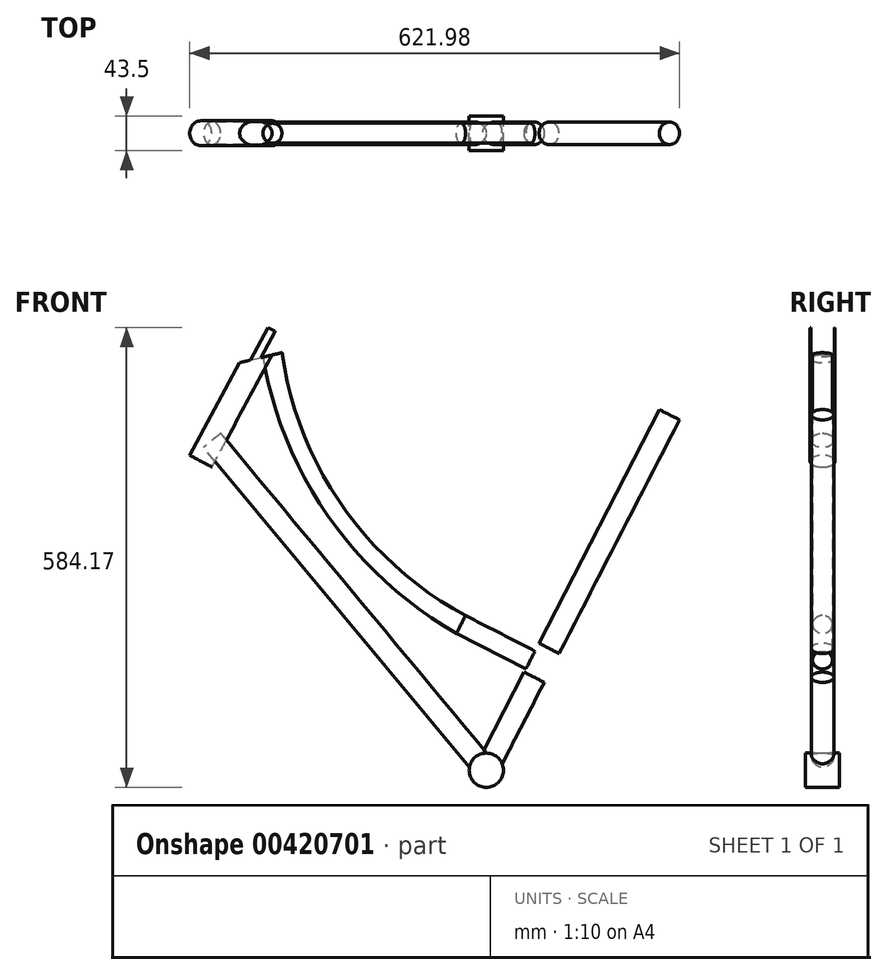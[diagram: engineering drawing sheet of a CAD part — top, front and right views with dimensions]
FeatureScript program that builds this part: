
annotation { "Feature Type Name" : "Feature", "Feature Type Description" : "" }
export const myFeature = defineFeature(function(context is Context, id is Id, definition is map)
    precondition{}
    {
        {
            var Q0;
            Q0=qCreatedBy(makeId("Front.planeOp"),FACE);
            var sketch = newSketch(context, id + "F0", { "sketchPlane" : qUnion([Q0])});
            skCircle(sketch, "E0", {"center": v(0, 0) * mm, "radius": 21.75 * mm});
            skSolve(sketch);
        }
        {
            var Q0;
            Q0=makeQuery(id+"F0.imprint","IMPRINT",FACE,{"disambiguationData":[TD([[makeQuery(id+"F0.imprint","IMPRINT",EDGE,{"derivedFrom":sQuery(id+"F0.wireOp",EDGE,"E0")}),1.0]])]});
            extrude(context, id + "F1", {"entities" : qUnion([Q0]), "depth" : 21.75 * mm});
        }
        {
            var Q0;
            Q0=makeQuery(id+"F1.opExtrude","CAP_FACE",FACE,{"disambiguationData":[OSD([sQuery(id+"F0.wireOp",EDGE,"E0")])],"isStart":true});
            extrude(context, id + "F2", {"entities" : qUnion([Q0]), "operationType" : NewBodyOperationType.ADD, "depth" : 21.75 * mm});
        }
        {
            var Q0;
            Q0=qCreatedBy(makeId("Front.planeOp"),FACE);
            var sketch = newSketch(context, id + "F3", { "sketchPlane" : qUnion([Q0])});
            skLineSegment(sketch, "E1", {"start": v(0, 0) * mm, "end": v(164.55, 0) * mm, "construction": true});
            skLineSegment(sketch, "E2", {"start": v(0, 0) * mm, "end": v(232.6, 451.62) * mm, "construction": true});
            skLineSegment(sketch, "E3", {"start": v(0, 0) * mm, "end": v(-348.5, 419.02) * mm, "construction": true});
            skLineSegment(sketch, "E4", {"start": v(-362.7, 392.6) * mm, "end": v(-272.76, 559.96) * mm, "construction": true});
            skPoint(sketch, "E5.end.orphan", {"position": v(68.68, 133.35) * mm});
            skPoint(sketch, "E5.start.orphan", {"position": v(-275.13, 555.56) * mm});
            skLineSegment(sketch, "E6", {"start": v(68.68, 133.35) * mm, "end": v(-32.16, 185.29) * mm, "construction": true});
            skArc(sketch, "E7", {"start": v(-275.13, 555.56) * mm, "mid": v(-202.35, 338.46) * mm, "end": v(-32.16, 185.29) * mm, "construction": true});
            skSolve(sketch);
        }
        {
            var Q0;
            Q0=sQuery(id+"F3.wireOp",VERTEX,"E2.end");
            var Q1;
            Q1=sQuery(id+"F3.wireOp",EDGE,"E2");
            cPlane(context, id + "F4", {"entities" : qUnion([Q0, Q1]), "cplaneType" : CPlaneType.LINE_POINT, "offset" : 25 * mm, "width" : 150 * mm, "height" : 150 * mm});
        }
        {
            var Q0;
            Q0=qCreatedBy(id+"F4.planeOp",FACE);
            var sketch = newSketch(context, id + "F5", { "sketchPlane" : qUnion([Q0])});
            skCircle(sketch, "E8", {"center": v(0, 0) * mm, "radius": 14.29 * mm});
            skSolve(sketch);
        }
        {
            var Q0;
            Q0 = qSketchRegion(id + "F5", true);
            extrude(context, id + "F6", {"entities" : qUnion([Q0]), "endBound" : BoundingType.UP_TO_NEXT, "oppositeDirection" : true, "depth" : 25 * mm});
        }
        {
            var Q0;
            Q0=sQuery(id+"F3.wireOp",VERTEX,"E4.end");
            var Q1;
            Q1=sQuery(id+"F3.wireOp",EDGE,"E4");
            cPlane(context, id + "F7", {"entities" : qUnion([Q0, Q1]), "cplaneType" : CPlaneType.LINE_POINT, "offset" : 25 * mm, "width" : 150 * mm, "height" : 150 * mm});
        }
        {
            var Q0;
            Q0=qCreatedBy(id+"F7.planeOp",FACE);
            var sketch = newSketch(context, id + "F8", { "sketchPlane" : qUnion([Q0])});
            skCircle(sketch, "E9", {"center": v(-505.32, 0) * mm, "radius": 15.88 * mm});
            skSolve(sketch);
        }
        {
            var Q0;
            Q0=makeQuery(id+"F8.imprint","IMPRINT",FACE,{"disambiguationData":[TD([[makeQuery(id+"F8.imprint","IMPRINT",EDGE,{"derivedFrom":sQuery(id+"F8.wireOp",EDGE,"E9")}),1.0]])]});
            extrude(context, id + "F9", {"entities" : qUnion([Q0]), "oppositeDirection" : true, "depth" : 190 * mm});
        }
        {
            var Q0;
            Q0=sQuery(id+"F3.wireOp",VERTEX,"E3.end");
            var Q1;
            Q1=sQuery(id+"F3.wireOp",EDGE,"E3");
            cPlane(context, id + "F10", {"entities" : qUnion([Q0, Q1]), "cplaneType" : CPlaneType.LINE_POINT, "offset" : 25 * mm, "width" : 150 * mm, "height" : 150 * mm});
        }
        {
            var Q0;
            Q0=qCreatedBy(id+"F10.planeOp",FACE);
            var sketch = newSketch(context, id + "F11", { "sketchPlane" : qUnion([Q0])});
            skCircle(sketch, "E10", {"center": v(0, 0) * mm, "radius": 14.29 * mm});
            skSolve(sketch);
        }
        {
            var Q0;
            Q0 = qSketchRegion(id + "F11", true);
            var Q1;
            {var subQ0=sQuery(id+"F0.wireOp",EDGE,"E0");Q1=makeQuery(id+"F2.boolean.opBoolean","MERGE",FACE,{"derivedFrom":[makeQuery(id+"F1.opExtrude","SWEPT_FACE",FACE,{"disambiguationData":[OSD([subQ0])]}),makeQuery(id+"F2.opExtrude","SWEPT_FACE",FACE,{"disambiguationData":[OSD([subQ0])]})]});}
            extrude(context, id + "F12", {"entities" : qUnion([Q0]), "endBound" : BoundingType.UP_TO_SURFACE, "oppositeDirection" : true, "endBoundEntityFace" : qUnion([Q1]), "depth" : 25 * mm});
        }
        {
            var Q0;
            Q0=sQuery(id+"F3.wireOp",VERTEX,"E5.start.orphan");
            var Q1;
            Q1=sQuery(id+"F3.wireOp",EDGE,"E7");
            cPlane(context, id + "F13", {"entities" : qUnion([Q0, Q1]), "cplaneType" : CPlaneType.CURVE_POINT, "offset" : 25 * mm, "width" : 150 * mm, "height" : 150 * mm});
        }
        {
            var Q0;
            Q0=sQuery(id+"F3.wireOp",VERTEX,"E7.end");
            var Q1;
            Q1=sQuery(id+"F3.wireOp",EDGE,"E7");
            cPlane(context, id + "F14", {"entities" : qUnion([Q0, Q1]), "cplaneType" : CPlaneType.CURVE_POINT, "offset" : 25 * mm, "width" : 150 * mm, "height" : 150 * mm});
        }
        {
            var Q0;
            Q0=qCreatedBy(id+"F13.planeOp",FACE);
            var sketch = newSketch(context, id + "F15", { "sketchPlane" : qUnion([Q0])});
            skCircle(sketch, "E11", {"center": v(-237.75, 0) * mm, "radius": 12.7 * mm});
            skSolve(sketch);
        }
        {
            var Q0;
            Q0=qCreatedBy(id+"F14.planeOp",FACE);
            var sketch = newSketch(context, id + "F16", { "sketchPlane" : qUnion([Q0])});
            skCircle(sketch, "E12", {"center": v(0, 150) * mm, "radius": 12.7 * mm});
            skSolve(sketch);
        }
        {
            var Q0;
            Q0=qCreatedBy(makeId("Front.planeOp"),FACE);
            var sketch = newSketch(context, id + "F17", { "sketchPlane" : qUnion([Q0])});
            skArc(sketch, "E13", {"start": v(-262.46, 556.4) * mm, "mid": v(-190.2, 346.43) * mm, "end": v(-26.35, 196.58) * mm});
            skSolve(sketch);
        }
        {
            var Q0;
            Q0=makeQuery(id+"F15.imprint","IMPRINT",FACE,{"disambiguationData":[TD([[makeQuery(id+"F15.imprint","IMPRINT",EDGE,{"derivedFrom":sQuery(id+"F15.wireOp",EDGE,"E11")}),1.0]])]});
            var Q1;
            Q1=makeQuery(id+"F16.imprint","IMPRINT",FACE,{"disambiguationData":[TD([[makeQuery(id+"F16.imprint","IMPRINT",EDGE,{"derivedFrom":sQuery(id+"F16.wireOp",EDGE,"E12")}),1.0]])]});
            var Q2;
            Q2=sQuery(id+"F17.wireOp",EDGE,"E13");
            loft(context, id + "F18", {"addGuides" : true, "sheetProfilesArray" : [{ "sheetProfileEntities" : qUnion([Q0]) }, { "sheetProfileEntities" : qUnion([Q1]) }], "guidesArray" : [{ "guideEntities" : qUnion([Q2]), "guideDerivativeType" : LoftGuideDerivativeType.DEFAULT, "guideDerivativeMagnitude" : 1 }]});
        }
        {
            var Q0;
            Q0=makeQuery(id+"F18.opLoft","CAP_FACE",FACE,{"disambiguationData":[OSD([makeQuery(id+"F16.imprint","IMPRINT",FACE,{"disambiguationData":[TD([[makeQuery(id+"F16.imprint","IMPRINT",EDGE,{"derivedFrom":sQuery(id+"F16.wireOp",EDGE,"E12")}),1.0]])]})])],"isStart":true});
            extrude(context, id + "F19", {"entities" : qUnion([Q0]), "operationType" : NewBodyOperationType.ADD, "endBound" : BoundingType.UP_TO_NEXT, "depth" : 25 * mm});
        }
        {
            var Q0;
            Q0=qCreatedBy(makeId("Front.planeOp"),FACE);
            var sketch = newSketch(context, id + "F20", { "sketchPlane" : qUnion([Q0])});
            skLineSegment(sketch, "E14", {"start": v(48.13, 124.66) * mm, "end": v(73.54, 111.58) * mm});
            skLineSegment(sketch, "E15", {"start": v(73.54, 111.58) * mm, "end": v(92.4, 148.21) * mm});
            skLineSegment(sketch, "E16", {"start": v(92.4, 148.21) * mm, "end": v(67, 161.3) * mm});
            skLineSegment(sketch, "E17", {"start": v(67, 161.3) * mm, "end": v(48.13, 124.66) * mm});
            skSolve(sketch);
        }
        {
            var Q0;
            Q0 = qSketchRegion(id + "F20", true);
            extrude(context, id + "F21", {"entities" : qUnion([Q0]), "operationType" : NewBodyOperationType.REMOVE, "endBound" : BoundingType.SYMMETRIC, "oppositeDirection" : true, "depth" : 30 * mm});
        }
        {
            var Q0;
            Q0=qCreatedBy(makeId("Front.planeOp"),FACE);
            var sketch = newSketch(context, id + "F22", { "sketchPlane" : qUnion([Q0])});
            skLineSegment(sketch, "E18", {"start": v(-434.42, 489.44) * mm, "end": v(-248.6, 533.01) * mm});
            skLineSegment(sketch, "E19", {"start": v(-248.6, 533.01) * mm, "end": v(-263.72, 603.92) * mm});
            skLineSegment(sketch, "E20", {"start": v(-263.72, 603.92) * mm, "end": v(-444.24, 547.61) * mm});
            skLineSegment(sketch, "E21", {"start": v(-444.24, 547.61) * mm, "end": v(-434.42, 489.44) * mm});
            skSolve(sketch);
        }
        {
            var Q0;
            Q0=makeQuery(id+"F22.imprint","IMPRINT",FACE,{"disambiguationData":[TD([[makeQuery(id+"F22.imprint","IMPRINT",EDGE,{"derivedFrom":sQuery(id+"F22.wireOp",EDGE,"E18")}),1.0]])]});
            extrude(context, id + "F23", {"entities" : qUnion([Q0]), "operationType" : NewBodyOperationType.REMOVE, "endBound" : BoundingType.SYMMETRIC, "oppositeDirection" : true, "depth" : 30 * mm});
        }
    });
